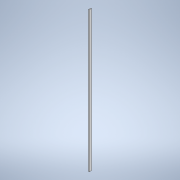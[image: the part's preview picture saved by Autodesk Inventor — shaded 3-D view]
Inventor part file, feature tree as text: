
AUTODESK INVENTOR PART (.ipt)
format: ipt  version: 2021 (Build 250183000, 183)  size: 93,696 bytes
history: native  units: mm
features: extrude x1, sketch x1
ambient origin geometry x8: Origin, YZ Plane, XZ Plane, XY Plane, X Axis, Y Axis, Z Axis, Center Point
bodies: Solid1 (feature_tree)
feature tree (2):
  extrude  "Extrusion1"  Depth=30.0mm
  sketch  "Sketch1"  dims[d0=10.0mm d1=30.0mm d2=1944.0mm d3=0.0mm]
